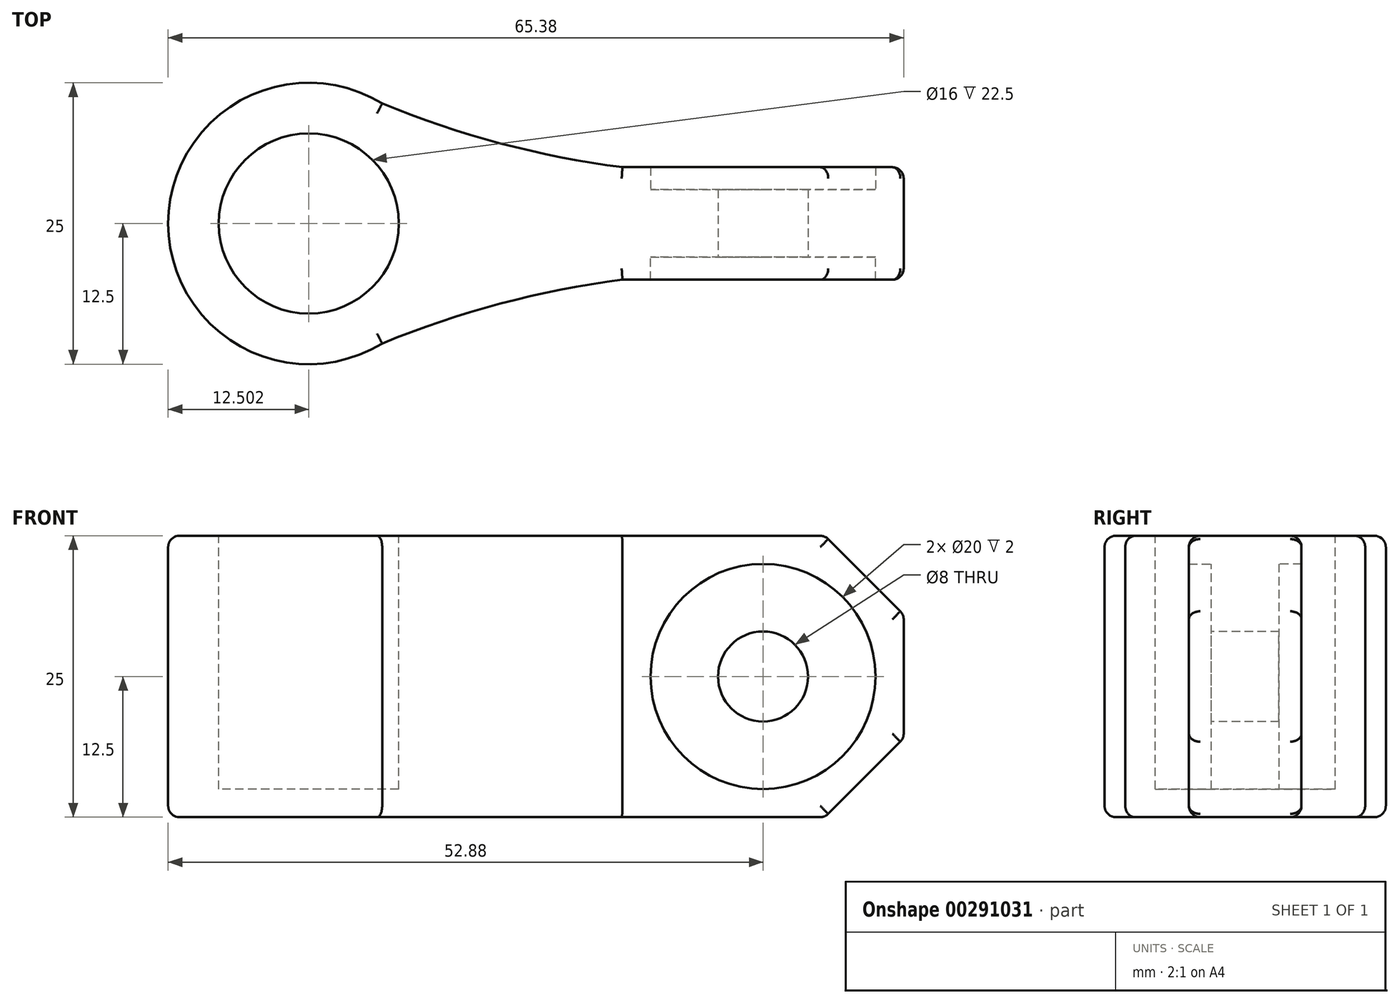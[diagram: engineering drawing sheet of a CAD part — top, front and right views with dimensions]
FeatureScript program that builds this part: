
annotation { "Feature Type Name" : "Feature", "Feature Type Description" : "" }
export const myFeature = defineFeature(function(context is Context, id is Id, definition is map)
    precondition{}
    {
        {
            var Q0;
            Q0=qCreatedBy(makeId("Front.planeOp"),FACE);
            var sketch = newSketch(context, id + "F0", { "sketchPlane" : qUnion([Q0])});
            skCircle(sketch, "E0", {"center": v(0, 0) * mm, "radius": 12.5 * mm});
            skSolve(sketch);
        }
        {
            var Q0;
            Q0 = qSketchRegion(id + "F0", true);
            extrude(context, id + "F1", {"entities" : qUnion([Q0]), "depth" : 3 * mm});
        }
        {
            var Q0;
            Q0=makeQuery(id+"F1.opExtrude","CAP_FACE",FACE,{"disambiguationData":[OSD([sQuery(id+"F0.wireOp",EDGE,"E0")])],"isStart":true});
            extrude(context, id + "F2", {"entities" : qUnion([Q0]), "operationType" : NewBodyOperationType.ADD, "depth" : 3 * mm});
        }
        {
            var Q0;
            Q0=makeQuery(id+"F2.opExtrude","CAP_FACE",FACE,{"disambiguationData":[OSD([sQuery(id+"F0.wireOp",EDGE,"E0")])],"isStart":false});
            var sketch = newSketch(context, id + "F3", { "sketchPlane" : qUnion([Q0])});
            skCircle(sketch, "E1", {"center": v(0, 0) * mm, "radius": 10 * mm});
            skSolve(sketch);
        }
        {
            var Q0;
            Q0=makeQuery(id+"F3.imprint","IMPRINT",FACE,{"disambiguationData":[TD([[makeQuery(id+"F3.imprint","IMPRINT",EDGE,{"derivedFrom":sQuery(id+"F3.wireOp",EDGE,"E1")}),-1.0]])]});
            extrude(context, id + "F4", {"entities" : qUnion([Q0]), "operationType" : NewBodyOperationType.ADD, "depth" : 2 * mm});
        }
        {
            var Q0;
            Q0=makeQuery(id+"F1.opExtrude","CAP_FACE",FACE,{"disambiguationData":[OSD([sQuery(id+"F0.wireOp",EDGE,"E0")])],"isStart":false});
            var sketch = newSketch(context, id + "F5", { "sketchPlane" : qUnion([Q0])});
            skCircle(sketch, "E2", {"center": v(0, 0) * mm, "radius": 10 * mm});
            skSolve(sketch);
        }
        {
            var Q0;
            Q0=makeQuery(id+"F5.imprint","IMPRINT",FACE,{"disambiguationData":[TD([[makeQuery(id+"F5.imprint","IMPRINT",EDGE,{"derivedFrom":sQuery(id+"F5.wireOp",EDGE,"E2")}),-1.0]])]});
            extrude(context, id + "F6", {"entities" : qUnion([Q0]), "operationType" : NewBodyOperationType.ADD, "depth" : 2 * mm});
        }
        {
            var Q0;
            Q0=makeQuery(id+"F1.opExtrude","CAP_FACE",FACE,{"disambiguationData":[OSD([sQuery(id+"F0.wireOp",EDGE,"E0")])],"isStart":false});
            var sketch = newSketch(context, id + "F7", { "sketchPlane" : qUnion([Q0])});
            skCircle(sketch, "E3", {"center": v(0, 0) * mm, "radius": 4 * mm});
            skSolve(sketch);
        }
        {
            var Q0;
            Q0 = qSketchRegion(id + "F7", true);
            extrude(context, id + "F8", {"entities" : qUnion([Q0]), "operationType" : NewBodyOperationType.REMOVE, "oppositeDirection" : true, "depth" : 15.9 * mm});
        }
        {
            var Q0;
            Q0=qCreatedBy(makeId("Top.planeOp"),FACE);
            var sketch = newSketch(context, id + "F9", { "sketchPlane" : qUnion([Q0])});
            skCircle(sketch, "E4", {"center": v(-40.38, 0) * mm, "radius": 12.5 * mm});
            skSolve(sketch);
        }
        {
            var Q0;
            Q0=makeQuery(id+"F9.imprint","IMPRINT",FACE,{"disambiguationData":[TD([[makeQuery(id+"F9.imprint","IMPRINT",EDGE,{"derivedFrom":sQuery(id+"F9.wireOp",EDGE,"E4")}),1.0]])]});
            extrude(context, id + "F10", {"entities" : qUnion([Q0]), "depth" : 12.5 * mm});
        }
        {
            var Q0;
            Q0=makeQuery(id+"F10.opExtrude","CAP_FACE",FACE,{"disambiguationData":[OSD([sQuery(id+"F9.wireOp",EDGE,"E4")])],"isStart":true});
            extrude(context, id + "F11", {"entities" : qUnion([Q0]), "operationType" : NewBodyOperationType.ADD, "depth" : 12.5 * mm});
        }
        {
            var Q0;
            Q0=makeQuery(id+"F10.opExtrude","CAP_FACE",FACE,{"disambiguationData":[OSD([sQuery(id+"F9.wireOp",EDGE,"E4")])],"isStart":false});
            var sketch = newSketch(context, id + "F12", { "sketchPlane" : qUnion([Q0])});
            skCircle(sketch, "E5", {"center": v(-40.38, 0) * mm, "radius": 8 * mm});
            skSolve(sketch);
        }
        {
            var Q0;
            Q0=makeQuery(id+"F12.imprint","IMPRINT",FACE,{"disambiguationData":[TD([[makeQuery(id+"F12.imprint","IMPRINT",EDGE,{"derivedFrom":sQuery(id+"F12.wireOp",EDGE,"E5")}),1.0]])]});
            extrude(context, id + "F13", {"entities" : qUnion([Q0]), "operationType" : NewBodyOperationType.REMOVE, "oppositeDirection" : true, "depth" : 22.5 * mm});
        }
        {
            var Q0;
            Q0=makeQuery(id+"F10.opExtrude","CAP_FACE",FACE,{"disambiguationData":[OSD([sQuery(id+"F9.wireOp",EDGE,"E4")])],"isStart":false});
            var sketch = newSketch(context, id + "F14", { "sketchPlane" : qUnion([Q0])});
            skArc(sketch, "E6.0", {"start": v(-33.85, -10.66) * mm, "mid": v(-27.88, 0) * mm, "end": v(-33.85, 10.66) * mm});
            skLineSegment(sketch, "E7.0", {"start": v(0, 5) * mm, "end": v(-12.5, 5) * mm});
            skLineSegment(sketch, "E8.0", {"start": v(0, -5) * mm, "end": v(-12.5, -5) * mm});
            skLineSegment(sketch, "E9", {"start": v(0, 5) * mm, "end": v(0, -5) * mm});
            skPoint(sketch, "E10.orphan", {"position": v(12.5, -5) * mm});
            skPoint(sketch, "E11.orphan", {"position": v(12.5, 5) * mm});
            skArc(sketch, "E12", {"start": v(-33.85, 10.66) * mm, "mid": v(-23.36, 7.13) * mm, "end": v(-12.5, 5) * mm});
            skPoint(sketch, "E13.endSnap0", {"position": v(-33.85, 0) * mm});
            skArc(sketch, "E14.MirrorCS", {"start": v(-33.85, -10.66) * mm, "mid": v(-23.36, -7.13) * mm, "end": v(-12.5, -5) * mm});
            skSolve(sketch);
        }
        {
            var Q0;
            Q0 = qSketchRegion(id + "F14", true);
            var Q1;
            Q1=sQuery(id+"F14.wireOp",EDGE,"Rn6MPZEb-hqg0-dPwA-YSnt-DKrFDszoGR8u");
            extrude(context, id + "F15", {"entities" : qUnion([Q0]), "operationType" : NewBodyOperationType.ADD, "surfaceEntities" : qUnion([Q1]), "oppositeDirection" : true, "depth" : 25 * mm});
        }
        {
            var Q0;
            Q0=makeQuery(id+"F4.opExtrude","CAP_FACE",FACE,{"disambiguationData":[OSD([sQuery(id+"F0.wireOp",EDGE,"E0"),sQuery(id+"F3.wireOp",EDGE,"E1")])],"isStart":false});
            var sketch = newSketch(context, id + "F16", { "sketchPlane" : qUnion([Q0])});
            skCircle(sketch, "E15.0", {"center": v(0, 0) * mm, "radius": 10 * mm});
            skSolve(sketch);
        }
        {
            var Q0;
            Q0 = qSketchRegion(id + "F16", true);
            extrude(context, id + "F17", {"entities" : qUnion([Q0]), "operationType" : NewBodyOperationType.REMOVE, "oppositeDirection" : true, "depth" : 2 * mm});
        }
        {
            var Q0;
            Q0=makeQuery(id+"F17.boolean.opBoolean","MERGE",FACE,{"derivedFrom":[makeQuery(id+"F2.opExtrude","CAP_FACE",FACE,{"disambiguationData":[OSD([sQuery(id+"F0.wireOp",EDGE,"E0")])],"isStart":false}),makeQuery(id+"F17.opExtrude","CAP_FACE",FACE,{"disambiguationData":[OSD([sQuery(id+"F16.wireOp",EDGE,"E15.0")])],"isStart":false})]});
            var sketch = newSketch(context, id + "F18", { "sketchPlane" : qUnion([Q0])});
            skArc(sketch, "E16.0", {"start": v(0, -4) * mm, "mid": v(-4, 0) * mm, "end": v(0, 4) * mm});
            skArc(sketch, "E17.MirrorCS", {"start": v(0, -4) * mm, "mid": v(4, 0) * mm, "end": v(0, 4) * mm});
            skSolve(sketch);
        }
        {
            var Q0;
            Q0 = qSketchRegion(id + "F18", true);
            extrude(context, id + "F19", {"entities" : qUnion([Q0]), "operationType" : NewBodyOperationType.REMOVE, "oppositeDirection" : true, "depth" : 25 * mm});
        }
        {
            var Q0;
            Q0=makeQuery(id+"F15.boolean.opBoolean","MERGE",FACE,{"derivedFrom":[makeQuery(id+"F6.opExtrude","CAP_FACE",FACE,{"disambiguationData":[OSD([sQuery(id+"F0.wireOp",EDGE,"E0"),sQuery(id+"F5.wireOp",EDGE,"E2")])],"isStart":false}),makeQuery(id+"F15.opExtrude","SWEPT_FACE",FACE,{"disambiguationData":[OSD([sQuery(id+"F14.wireOp",EDGE,"E8.0")])]})]});
            var sketch = newSketch(context, id + "F20", { "sketchPlane" : qUnion([Q0])});
            skCircle(sketch, "E18.0", {"center": v(0, 0) * mm, "radius": 10 * mm});
            skSolve(sketch);
        }
        {
            var Q0;
            Q0 = qSketchRegion(id + "F20", true);
            extrude(context, id + "F21", {"entities" : qUnion([Q0]), "operationType" : NewBodyOperationType.REMOVE, "oppositeDirection" : true, "depth" : 2 * mm});
        }
        {
            var Q0;
            Q0=makeQuery(id+"F15.boolean.opBoolean","MERGE",FACE,{"derivedFrom":[makeQuery(id+"F6.opExtrude","CAP_FACE",FACE,{"disambiguationData":[OSD([sQuery(id+"F0.wireOp",EDGE,"E0"),sQuery(id+"F5.wireOp",EDGE,"E2")])],"isStart":false}),makeQuery(id+"F15.opExtrude","SWEPT_FACE",FACE,{"disambiguationData":[OSD([sQuery(id+"F14.wireOp",EDGE,"E8.0")])]})]});
            var sketch = newSketch(context, id + "F22", { "sketchPlane" : qUnion([Q0])});
            skLineSegment(sketch, "E19", {"start": v(0, 12.5) * mm, "end": v(12.5, 12.5) * mm});
            skPoint(sketch, "E19.endSnap0", {"position": v(12.5, 0) * mm});
            skLineSegment(sketch, "E20", {"start": v(12.5, 12.5) * mm, "end": v(12.5, -12.5) * mm});
            skLineSegment(sketch, "E21", {"start": v(12.5, -12.5) * mm, "end": v(0, -12.5) * mm});
            skSolve(sketch);
        }
        {
            var Q0;
            {var subQ0=sQuery(id+"F22.wireOp",EDGE,"E19");Q0=makeQuery(id+"F22.imprint","IMPRINT",FACE,{"disambiguationData":[TD([[makeQuery(id+"F22.imprint","IMPRINT",EDGE,{"derivedFrom":subQ0}),-1.0]])]});}
            var Q1;
            {var subQ0=sQuery(id+"F22.wireOp",EDGE,"E21");Q1=makeQuery(id+"F22.imprint","IMPRINT",FACE,{"disambiguationData":[TD([[makeQuery(id+"F22.imprint","IMPRINT",EDGE,{"derivedFrom":subQ0}),-1.0]])]});}
            extrude(context, id + "F23", {"entities" : qUnion([Q0, Q1]), "operationType" : NewBodyOperationType.ADD, "oppositeDirection" : true, "depth" : 10 * mm});
        }
        {
            var Q0;
            Q0=makeQuery(id+"F23.opExtrude","SWEPT_EDGE",EDGE,{"disambiguationData":[OSD([sQuery(id+"F22.wireOp",EDGE,"E19"),sQuery(id+"F22.wireOp",EDGE,"E20")])]});
            chamfer(context, id + "F24", {"entities" : qUnion([Q0]), "width" : 7 * mm, "tangentPropagation" : true});
        }
        {
            var Q0;
            Q0=makeQuery(id+"F23.opExtrude","SWEPT_EDGE",EDGE,{"disambiguationData":[OSD([sQuery(id+"F22.wireOp",EDGE,"E20"),sQuery(id+"F22.wireOp",EDGE,"E21")])]});
            chamfer(context, id + "F25", {"entities" : qUnion([Q0]), "width" : 7 * mm, "tangentPropagation" : true});
        }
        {
            var Q0;
            Q0=makeQuery(id+"F10.opExtrude","CAP_EDGE",EDGE,{"disambiguationData":[OSD([sQuery(id+"F9.wireOp",EDGE,"E4")])],"isStart":false});
            var Q1;
            Q1=makeQuery(id+"F15.opExtrude","CAP_EDGE",EDGE,{"disambiguationData":[OSD([sQuery(id+"F14.wireOp",EDGE,"E14.MirrorCS")])],"isStart":true});
            var Q2;
            Q2=makeQuery(id+"F23.boolean.opBoolean","MERGE",EDGE,{"derivedFrom":[makeQuery(id+"F15.opExtrude","CAP_EDGE",EDGE,{"disambiguationData":[OSD([sQuery(id+"F14.wireOp",EDGE,"E8.0")])],"isStart":true}),makeQuery(id+"F23.opExtrude","CAP_EDGE",EDGE,{"disambiguationData":[OSD([sQuery(id+"F22.wireOp",EDGE,"E19")])],"isStart":true})]});
            var Q3;
            {var subQ0=sQuery(id+"F22.wireOp",EDGE,"E20");var subQ1=sQuery(id+"F0.wireOp",EDGE,"E0");var subQ2=sQuery(id+"F22.wireOp",EDGE,"E19");Q3=makeQuery(id+"F24.opChamfer","BLEND_EDGE",EDGE,{"blendedFrom":[makeQuery(id+"F23.opExtrude","SWEPT_EDGE",EDGE,{"disambiguationData":[OSD([subQ2,subQ0])]}),makeQuery(id+"F23.boolean.opBoolean","MERGE",FACE,{"derivedFrom":[makeQuery(id+"F15.boolean.opBoolean","MERGE",FACE,{"derivedFrom":[makeQuery(id+"F6.opExtrude","CAP_FACE",FACE,{"disambiguationData":[OSD([subQ1,sQuery(id+"F5.wireOp",EDGE,"E2")])],"isStart":false}),makeQuery(id+"F15.opExtrude","SWEPT_FACE",FACE,{"disambiguationData":[OSD([sQuery(id+"F14.wireOp",EDGE,"E8.0")])]})]}),makeQuery(id+"F23.opExtrude","CAP_FACE",FACE,{"disambiguationData":[OSD([subQ1,subQ2,subQ0])],"isStart":true}),makeQuery(id+"F23.opExtrude","CAP_FACE",FACE,{"disambiguationData":[OSD([subQ1,subQ0,sQuery(id+"F22.wireOp",EDGE,"E21")])],"isStart":true})]})],"blendedInto":[makeQuery(id+"F23.boolean.opBoolean","MERGE",FACE,{"derivedFrom":[makeQuery(id+"F15.boolean.opBoolean","MERGE",FACE,{"derivedFrom":[makeQuery(id+"F6.opExtrude","CAP_FACE",FACE,{"disambiguationData":[OSD([subQ1,sQuery(id+"F5.wireOp",EDGE,"E2")])],"isStart":false}),makeQuery(id+"F15.opExtrude","SWEPT_FACE",FACE,{"disambiguationData":[OSD([sQuery(id+"F14.wireOp",EDGE,"E8.0")])]})]}),makeQuery(id+"F23.opExtrude","CAP_FACE",FACE,{"disambiguationData":[OSD([subQ1,subQ2,subQ0])],"isStart":true}),makeQuery(id+"F23.opExtrude","CAP_FACE",FACE,{"disambiguationData":[OSD([subQ1,subQ0,sQuery(id+"F22.wireOp",EDGE,"E21")])],"isStart":true})]})]});}
            var Q4;
            {var subQ0=sQuery(id+"F22.wireOp",EDGE,"E20");Q4=makeQuery(id+"F23.boolean.opBoolean","MERGE",EDGE,{"derivedFrom":[makeQuery(id+"F23.opExtrude","CAP_EDGE",EDGE,{"disambiguationData":[OSD([subQ0]),TDD([makeQuery(id+"F22.imprint","IMPRINT",EDGE,{"disambiguationData":[TD([[makeQuery(id+"F22.imprint","INTERSECT",VERTEX,{"derivedFrom":[sQuery(id+"F22.wireOp",EDGE,"E19"),subQ0]}),-1.0]])],"derivedFrom":subQ0})])],"isStart":true}),makeQuery(id+"F23.opExtrude","CAP_EDGE",EDGE,{"disambiguationData":[OSD([subQ0]),TDD([makeQuery(id+"F22.imprint","IMPRINT",EDGE,{"disambiguationData":[TD([[makeQuery(id+"F22.imprint","INTERSECT",VERTEX,{"derivedFrom":[subQ0,sQuery(id+"F22.wireOp",EDGE,"E21")]}),1.0]])],"derivedFrom":subQ0})])],"isStart":true})]});}
            var Q5;
            {var subQ0=sQuery(id+"F22.wireOp",EDGE,"E21");var subQ1=sQuery(id+"F22.wireOp",EDGE,"E20");var subQ2=sQuery(id+"F0.wireOp",EDGE,"E0");Q5=makeQuery(id+"F25.opChamfer","BLEND_EDGE",EDGE,{"blendedFrom":[makeQuery(id+"F23.opExtrude","SWEPT_EDGE",EDGE,{"disambiguationData":[OSD([subQ1,subQ0])]}),makeQuery(id+"F23.boolean.opBoolean","MERGE",FACE,{"derivedFrom":[makeQuery(id+"F15.boolean.opBoolean","MERGE",FACE,{"derivedFrom":[makeQuery(id+"F6.opExtrude","CAP_FACE",FACE,{"disambiguationData":[OSD([subQ2,sQuery(id+"F5.wireOp",EDGE,"E2")])],"isStart":false}),makeQuery(id+"F15.opExtrude","SWEPT_FACE",FACE,{"disambiguationData":[OSD([sQuery(id+"F14.wireOp",EDGE,"E8.0")])]})]}),makeQuery(id+"F23.opExtrude","CAP_FACE",FACE,{"disambiguationData":[OSD([subQ2,sQuery(id+"F22.wireOp",EDGE,"E19"),subQ1])],"isStart":true}),makeQuery(id+"F23.opExtrude","CAP_FACE",FACE,{"disambiguationData":[OSD([subQ2,subQ1,subQ0])],"isStart":true})]})],"blendedInto":[makeQuery(id+"F23.boolean.opBoolean","MERGE",FACE,{"derivedFrom":[makeQuery(id+"F15.boolean.opBoolean","MERGE",FACE,{"derivedFrom":[makeQuery(id+"F6.opExtrude","CAP_FACE",FACE,{"disambiguationData":[OSD([subQ2,sQuery(id+"F5.wireOp",EDGE,"E2")])],"isStart":false}),makeQuery(id+"F15.opExtrude","SWEPT_FACE",FACE,{"disambiguationData":[OSD([sQuery(id+"F14.wireOp",EDGE,"E8.0")])]})]}),makeQuery(id+"F23.opExtrude","CAP_FACE",FACE,{"disambiguationData":[OSD([subQ2,sQuery(id+"F22.wireOp",EDGE,"E19"),subQ1])],"isStart":true}),makeQuery(id+"F23.opExtrude","CAP_FACE",FACE,{"disambiguationData":[OSD([subQ2,subQ1,subQ0])],"isStart":true})]})]});}
            var Q6;
            Q6=makeQuery(id+"F23.boolean.opBoolean","MERGE",EDGE,{"derivedFrom":[makeQuery(id+"F15.opExtrude","CAP_EDGE",EDGE,{"disambiguationData":[OSD([sQuery(id+"F14.wireOp",EDGE,"E8.0")])],"isStart":false}),makeQuery(id+"F23.opExtrude","CAP_EDGE",EDGE,{"disambiguationData":[OSD([sQuery(id+"F22.wireOp",EDGE,"E21")])],"isStart":true})]});
            var Q7;
            Q7=makeQuery(id+"F15.opExtrude","CAP_EDGE",EDGE,{"disambiguationData":[OSD([sQuery(id+"F14.wireOp",EDGE,"E14.MirrorCS")])],"isStart":false});
            var Q8;
            Q8=makeQuery(id+"F11.opExtrude","CAP_EDGE",EDGE,{"disambiguationData":[OSD([sQuery(id+"F9.wireOp",EDGE,"E4")])],"isStart":false});
            var Q9;
            Q9=makeQuery(id+"F15.opExtrude","CAP_EDGE",EDGE,{"disambiguationData":[OSD([sQuery(id+"F14.wireOp",EDGE,"E12")])],"isStart":true});
            var Q10;
            Q10=makeQuery(id+"F23.boolean.opBoolean","MERGE",EDGE,{"derivedFrom":[makeQuery(id+"F15.opExtrude","CAP_EDGE",EDGE,{"disambiguationData":[OSD([sQuery(id+"F14.wireOp",EDGE,"E7.0")])],"isStart":true}),makeQuery(id+"F23.opExtrude","CAP_EDGE",EDGE,{"disambiguationData":[OSD([sQuery(id+"F22.wireOp",EDGE,"E19")])],"isStart":false})]});
            var Q11;
            {var subQ0=sQuery(id+"F22.wireOp",EDGE,"E20");var subQ1=sQuery(id+"F0.wireOp",EDGE,"E0");var subQ2=sQuery(id+"F22.wireOp",EDGE,"E19");Q11=makeQuery(id+"F24.opChamfer","BLEND_EDGE",EDGE,{"blendedFrom":[makeQuery(id+"F23.opExtrude","SWEPT_EDGE",EDGE,{"disambiguationData":[OSD([subQ2,subQ0])]}),makeQuery(id+"F23.boolean.opBoolean","MERGE",FACE,{"derivedFrom":[makeQuery(id+"F15.boolean.opBoolean","MERGE",FACE,{"derivedFrom":[makeQuery(id+"F4.opExtrude","CAP_FACE",FACE,{"disambiguationData":[OSD([subQ1,sQuery(id+"F3.wireOp",EDGE,"E1")])],"isStart":false}),makeQuery(id+"F15.opExtrude","SWEPT_FACE",FACE,{"disambiguationData":[OSD([sQuery(id+"F14.wireOp",EDGE,"E7.0")])]})]}),makeQuery(id+"F23.opExtrude","CAP_FACE",FACE,{"disambiguationData":[OSD([subQ1,subQ2,subQ0])],"isStart":false}),makeQuery(id+"F23.opExtrude","CAP_FACE",FACE,{"disambiguationData":[OSD([subQ1,subQ0,sQuery(id+"F22.wireOp",EDGE,"E21")])],"isStart":false})]})],"blendedInto":[makeQuery(id+"F23.boolean.opBoolean","MERGE",FACE,{"derivedFrom":[makeQuery(id+"F15.boolean.opBoolean","MERGE",FACE,{"derivedFrom":[makeQuery(id+"F4.opExtrude","CAP_FACE",FACE,{"disambiguationData":[OSD([subQ1,sQuery(id+"F3.wireOp",EDGE,"E1")])],"isStart":false}),makeQuery(id+"F15.opExtrude","SWEPT_FACE",FACE,{"disambiguationData":[OSD([sQuery(id+"F14.wireOp",EDGE,"E7.0")])]})]}),makeQuery(id+"F23.opExtrude","CAP_FACE",FACE,{"disambiguationData":[OSD([subQ1,subQ2,subQ0])],"isStart":false}),makeQuery(id+"F23.opExtrude","CAP_FACE",FACE,{"disambiguationData":[OSD([subQ1,subQ0,sQuery(id+"F22.wireOp",EDGE,"E21")])],"isStart":false})]})]});}
            var Q12;
            Q12=makeQuery(id+"F15.opExtrude","CAP_EDGE",EDGE,{"disambiguationData":[OSD([sQuery(id+"F14.wireOp",EDGE,"E12")])],"isStart":false});
            var Q13;
            Q13=makeQuery(id+"F23.boolean.opBoolean","MERGE",EDGE,{"derivedFrom":[makeQuery(id+"F15.opExtrude","CAP_EDGE",EDGE,{"disambiguationData":[OSD([sQuery(id+"F14.wireOp",EDGE,"E7.0")])],"isStart":false}),makeQuery(id+"F23.opExtrude","CAP_EDGE",EDGE,{"disambiguationData":[OSD([sQuery(id+"F22.wireOp",EDGE,"E21")])],"isStart":false})]});
            var Q14;
            {var subQ0=sQuery(id+"F22.wireOp",EDGE,"E21");var subQ1=sQuery(id+"F22.wireOp",EDGE,"E20");var subQ2=sQuery(id+"F0.wireOp",EDGE,"E0");Q14=makeQuery(id+"F25.opChamfer","BLEND_EDGE",EDGE,{"blendedFrom":[makeQuery(id+"F23.opExtrude","SWEPT_EDGE",EDGE,{"disambiguationData":[OSD([subQ1,subQ0])]}),makeQuery(id+"F23.boolean.opBoolean","MERGE",FACE,{"derivedFrom":[makeQuery(id+"F15.boolean.opBoolean","MERGE",FACE,{"derivedFrom":[makeQuery(id+"F4.opExtrude","CAP_FACE",FACE,{"disambiguationData":[OSD([subQ2,sQuery(id+"F3.wireOp",EDGE,"E1")])],"isStart":false}),makeQuery(id+"F15.opExtrude","SWEPT_FACE",FACE,{"disambiguationData":[OSD([sQuery(id+"F14.wireOp",EDGE,"E7.0")])]})]}),makeQuery(id+"F23.opExtrude","CAP_FACE",FACE,{"disambiguationData":[OSD([subQ2,sQuery(id+"F22.wireOp",EDGE,"E19"),subQ1])],"isStart":false}),makeQuery(id+"F23.opExtrude","CAP_FACE",FACE,{"disambiguationData":[OSD([subQ2,subQ1,subQ0])],"isStart":false})]})],"blendedInto":[makeQuery(id+"F23.boolean.opBoolean","MERGE",FACE,{"derivedFrom":[makeQuery(id+"F15.boolean.opBoolean","MERGE",FACE,{"derivedFrom":[makeQuery(id+"F4.opExtrude","CAP_FACE",FACE,{"disambiguationData":[OSD([subQ2,sQuery(id+"F3.wireOp",EDGE,"E1")])],"isStart":false}),makeQuery(id+"F15.opExtrude","SWEPT_FACE",FACE,{"disambiguationData":[OSD([sQuery(id+"F14.wireOp",EDGE,"E7.0")])]})]}),makeQuery(id+"F23.opExtrude","CAP_FACE",FACE,{"disambiguationData":[OSD([subQ2,sQuery(id+"F22.wireOp",EDGE,"E19"),subQ1])],"isStart":false}),makeQuery(id+"F23.opExtrude","CAP_FACE",FACE,{"disambiguationData":[OSD([subQ2,subQ1,subQ0])],"isStart":false})]})]});}
            var Q15;
            {var subQ0=sQuery(id+"F22.wireOp",EDGE,"E20");Q15=makeQuery(id+"F23.boolean.opBoolean","MERGE",EDGE,{"derivedFrom":[makeQuery(id+"F23.opExtrude","CAP_EDGE",EDGE,{"disambiguationData":[OSD([subQ0]),TDD([makeQuery(id+"F22.imprint","IMPRINT",EDGE,{"disambiguationData":[TD([[makeQuery(id+"F22.imprint","INTERSECT",VERTEX,{"derivedFrom":[sQuery(id+"F22.wireOp",EDGE,"E19"),subQ0]}),-1.0]])],"derivedFrom":subQ0})])],"isStart":false}),makeQuery(id+"F23.opExtrude","CAP_EDGE",EDGE,{"disambiguationData":[OSD([subQ0]),TDD([makeQuery(id+"F22.imprint","IMPRINT",EDGE,{"disambiguationData":[TD([[makeQuery(id+"F22.imprint","INTERSECT",VERTEX,{"derivedFrom":[subQ0,sQuery(id+"F22.wireOp",EDGE,"E21")]}),1.0]])],"derivedFrom":subQ0})])],"isStart":false})]});}
            fillet(context, id + "F26", {"entities" : qUnion([Q0, Q1, Q2, Q3, Q4, Q5, Q6, Q7, Q8, Q9, Q10, Q11, Q12, Q13, Q14, Q15]), "radius" : 1 * mm, "tangentPropagation" : true, "allowEdgeOverflow" : false});
        }
        {
            var Q0;
            {var subQ0=sQuery(id+"F22.wireOp",EDGE,"E19");Q0=makeQuery(id+"F24.opChamfer","BLEND_EDGE",EDGE,{"blendedFrom":[makeQuery(id+"F23.opExtrude","SWEPT_EDGE",EDGE,{"disambiguationData":[OSD([subQ0,sQuery(id+"F22.wireOp",EDGE,"E20")])]}),makeQuery(id+"F23.boolean.opBoolean","MERGE",FACE,{"derivedFrom":[makeQuery(id+"F15.boolean.opBoolean","MERGE",FACE,{"derivedFrom":[makeQuery(id+"F10.opExtrude","CAP_FACE",FACE,{"disambiguationData":[OSD([sQuery(id+"F9.wireOp",EDGE,"E4")])],"isStart":false}),makeQuery(id+"F15.opExtrude","CAP_FACE",FACE,{"disambiguationData":[OSD([sQuery(id+"F14.wireOp",EDGE,"E6.0"),sQuery(id+"F14.wireOp",EDGE,"E7.0"),sQuery(id+"F14.wireOp",EDGE,"E8.0"),sQuery(id+"F14.wireOp",EDGE,"E9"),sQuery(id+"F14.wireOp",EDGE,"E12"),sQuery(id+"F14.wireOp",EDGE,"E14.MirrorCS")])],"isStart":true})]}),makeQuery(id+"F23.opExtrude","SWEPT_FACE",FACE,{"disambiguationData":[OSD([subQ0])]})]})],"blendedInto":[makeQuery(id+"F23.boolean.opBoolean","MERGE",FACE,{"derivedFrom":[makeQuery(id+"F15.boolean.opBoolean","MERGE",FACE,{"derivedFrom":[makeQuery(id+"F10.opExtrude","CAP_FACE",FACE,{"disambiguationData":[OSD([sQuery(id+"F9.wireOp",EDGE,"E4")])],"isStart":false}),makeQuery(id+"F15.opExtrude","CAP_FACE",FACE,{"disambiguationData":[OSD([sQuery(id+"F14.wireOp",EDGE,"E6.0"),sQuery(id+"F14.wireOp",EDGE,"E7.0"),sQuery(id+"F14.wireOp",EDGE,"E8.0"),sQuery(id+"F14.wireOp",EDGE,"E9"),sQuery(id+"F14.wireOp",EDGE,"E12"),sQuery(id+"F14.wireOp",EDGE,"E14.MirrorCS")])],"isStart":true})]}),makeQuery(id+"F23.opExtrude","SWEPT_FACE",FACE,{"disambiguationData":[OSD([subQ0])]})]})]});}
            var Q1;
            {var subQ0=sQuery(id+"F22.wireOp",EDGE,"E20");var subQ2=sQuery(id+"F22.wireOp",EDGE,"E19");Q1=makeQuery(id+"F24.opChamfer","BLEND_EDGE",EDGE,{"blendedFrom":[makeQuery(id+"F23.opExtrude","SWEPT_EDGE",EDGE,{"disambiguationData":[OSD([subQ2,subQ0])]}),makeQuery(id+"F23.boolean.opBoolean","MERGE",FACE,{"derivedFrom":[makeQuery(id+"F23.opExtrude","SWEPT_FACE",FACE,{"disambiguationData":[OSD([subQ0]),TDD([makeQuery(id+"F22.imprint","IMPRINT",EDGE,{"disambiguationData":[TD([[makeQuery(id+"F22.imprint","INTERSECT",VERTEX,{"derivedFrom":[subQ2,subQ0]}),-1.0]])],"derivedFrom":subQ0})])]}),makeQuery(id+"F23.opExtrude","SWEPT_FACE",FACE,{"disambiguationData":[OSD([subQ0]),TDD([makeQuery(id+"F22.imprint","IMPRINT",EDGE,{"disambiguationData":[TD([[makeQuery(id+"F22.imprint","INTERSECT",VERTEX,{"derivedFrom":[subQ0,sQuery(id+"F22.wireOp",EDGE,"E21")]}),1.0]])],"derivedFrom":subQ0})])]})]})],"blendedInto":[makeQuery(id+"F23.boolean.opBoolean","MERGE",FACE,{"derivedFrom":[makeQuery(id+"F23.opExtrude","SWEPT_FACE",FACE,{"disambiguationData":[OSD([subQ0]),TDD([makeQuery(id+"F22.imprint","IMPRINT",EDGE,{"disambiguationData":[TD([[makeQuery(id+"F22.imprint","INTERSECT",VERTEX,{"derivedFrom":[subQ2,subQ0]}),-1.0]])],"derivedFrom":subQ0})])]}),makeQuery(id+"F23.opExtrude","SWEPT_FACE",FACE,{"disambiguationData":[OSD([subQ0]),TDD([makeQuery(id+"F22.imprint","IMPRINT",EDGE,{"disambiguationData":[TD([[makeQuery(id+"F22.imprint","INTERSECT",VERTEX,{"derivedFrom":[subQ0,sQuery(id+"F22.wireOp",EDGE,"E21")]}),1.0]])],"derivedFrom":subQ0})])]})]})]});}
            var Q2;
            {var subQ0=sQuery(id+"F22.wireOp",EDGE,"E21");var subQ1=sQuery(id+"F22.wireOp",EDGE,"E20");Q2=makeQuery(id+"F25.opChamfer","BLEND_EDGE",EDGE,{"blendedFrom":[makeQuery(id+"F23.opExtrude","SWEPT_EDGE",EDGE,{"disambiguationData":[OSD([subQ1,subQ0])]}),makeQuery(id+"F23.boolean.opBoolean","MERGE",FACE,{"derivedFrom":[makeQuery(id+"F23.opExtrude","SWEPT_FACE",FACE,{"disambiguationData":[OSD([subQ1]),TDD([makeQuery(id+"F22.imprint","IMPRINT",EDGE,{"disambiguationData":[TD([[makeQuery(id+"F22.imprint","INTERSECT",VERTEX,{"derivedFrom":[sQuery(id+"F22.wireOp",EDGE,"E19"),subQ1]}),-1.0]])],"derivedFrom":subQ1})])]}),makeQuery(id+"F23.opExtrude","SWEPT_FACE",FACE,{"disambiguationData":[OSD([subQ1]),TDD([makeQuery(id+"F22.imprint","IMPRINT",EDGE,{"disambiguationData":[TD([[makeQuery(id+"F22.imprint","INTERSECT",VERTEX,{"derivedFrom":[subQ1,subQ0]}),1.0]])],"derivedFrom":subQ1})])]})]})],"blendedInto":[makeQuery(id+"F23.boolean.opBoolean","MERGE",FACE,{"derivedFrom":[makeQuery(id+"F23.opExtrude","SWEPT_FACE",FACE,{"disambiguationData":[OSD([subQ1]),TDD([makeQuery(id+"F22.imprint","IMPRINT",EDGE,{"disambiguationData":[TD([[makeQuery(id+"F22.imprint","INTERSECT",VERTEX,{"derivedFrom":[sQuery(id+"F22.wireOp",EDGE,"E19"),subQ1]}),-1.0]])],"derivedFrom":subQ1})])]}),makeQuery(id+"F23.opExtrude","SWEPT_FACE",FACE,{"disambiguationData":[OSD([subQ1]),TDD([makeQuery(id+"F22.imprint","IMPRINT",EDGE,{"disambiguationData":[TD([[makeQuery(id+"F22.imprint","INTERSECT",VERTEX,{"derivedFrom":[subQ1,subQ0]}),1.0]])],"derivedFrom":subQ1})])]})]})]});}
            var Q3;
            {var subQ0=sQuery(id+"F22.wireOp",EDGE,"E21");Q3=makeQuery(id+"F25.opChamfer","BLEND_EDGE",EDGE,{"blendedFrom":[makeQuery(id+"F23.opExtrude","SWEPT_EDGE",EDGE,{"disambiguationData":[OSD([sQuery(id+"F22.wireOp",EDGE,"E20"),subQ0])]}),makeQuery(id+"F23.boolean.opBoolean","MERGE",FACE,{"derivedFrom":[makeQuery(id+"F15.boolean.opBoolean","MERGE",FACE,{"derivedFrom":[makeQuery(id+"F11.opExtrude","CAP_FACE",FACE,{"disambiguationData":[OSD([sQuery(id+"F9.wireOp",EDGE,"E4")])],"isStart":false}),makeQuery(id+"F15.opExtrude","CAP_FACE",FACE,{"disambiguationData":[OSD([sQuery(id+"F14.wireOp",EDGE,"E6.0"),sQuery(id+"F14.wireOp",EDGE,"E7.0"),sQuery(id+"F14.wireOp",EDGE,"E8.0"),sQuery(id+"F14.wireOp",EDGE,"E9"),sQuery(id+"F14.wireOp",EDGE,"E12"),sQuery(id+"F14.wireOp",EDGE,"E14.MirrorCS")])],"isStart":false})]}),makeQuery(id+"F23.opExtrude","SWEPT_FACE",FACE,{"disambiguationData":[OSD([subQ0])]})]})],"blendedInto":[makeQuery(id+"F23.boolean.opBoolean","MERGE",FACE,{"derivedFrom":[makeQuery(id+"F15.boolean.opBoolean","MERGE",FACE,{"derivedFrom":[makeQuery(id+"F11.opExtrude","CAP_FACE",FACE,{"disambiguationData":[OSD([sQuery(id+"F9.wireOp",EDGE,"E4")])],"isStart":false}),makeQuery(id+"F15.opExtrude","CAP_FACE",FACE,{"disambiguationData":[OSD([sQuery(id+"F14.wireOp",EDGE,"E6.0"),sQuery(id+"F14.wireOp",EDGE,"E7.0"),sQuery(id+"F14.wireOp",EDGE,"E8.0"),sQuery(id+"F14.wireOp",EDGE,"E9"),sQuery(id+"F14.wireOp",EDGE,"E12"),sQuery(id+"F14.wireOp",EDGE,"E14.MirrorCS")])],"isStart":false})]}),makeQuery(id+"F23.opExtrude","SWEPT_FACE",FACE,{"disambiguationData":[OSD([subQ0])]})]})]});}
            fillet(context, id + "F27", {"entities" : qUnion([Q0, Q1, Q2, Q3]), "radius" : 1 * mm, "tangentPropagation" : true, "allowEdgeOverflow" : false});
        }
    });
